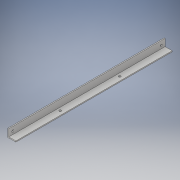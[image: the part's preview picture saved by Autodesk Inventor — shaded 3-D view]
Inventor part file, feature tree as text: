
AUTODESK INVENTOR PART (.ipt)
format: ipt  version: 2017 (Build 210142000, 142)  size: 124,928 bytes
history: native  units: in
note: dims shown in document units (in); Inventor stores cm internally (conversion verified against a paired STEP export)
features: hole x3, sketch x3, extrude x1
ambient origin geometry x8: Origin, YZ Plane, XZ Plane, XY Plane, X Axis, Y Axis, Z Axis, Center Point
bodies: Solid1 (feature_tree)
feature tree (7):
  extrude  "Extrusion1"  Depth=1.0in
  hole  "Hole4"  [1 undecoded]
  hole  "Hole5"  [1 undecoded]
  hole  "Hole6"  [1 undecoded]
  sketch  "Sketch7"  dims[d0=1.0in d1=1.0in]
  sketch  "Sketch8"  dims[d2=0.125in d3=19.375in d4=0.0in]
  sketch  "Sketch9"  dims[d43=0.5in d44=0.5in d45=0.7874in d47=18.375in d48=0.3937in d50=1.0in d52=0.266in d53=0.75in d54=0.507in d55=0.25in d56=0.5635in d57=1.0in d58=0.8108in d59=0.5in d60=6.0in d61=0.266in d62=0.75in d63=0.507in d64=0.25in d65=0.5635in d66=1.0in d67=0.8108in d68=0.5in d69=6.0in d70=0.266in d71=0.75in d72=0.507in d73=0.25in d74=0.5635in d75=1.0in d76=0.8108in]
note: 3 required parameter values undecoded (feature->parameter linkage not recoverable at this tier; creation-order binding heuristic only, values carry confidence <= 0.55)
